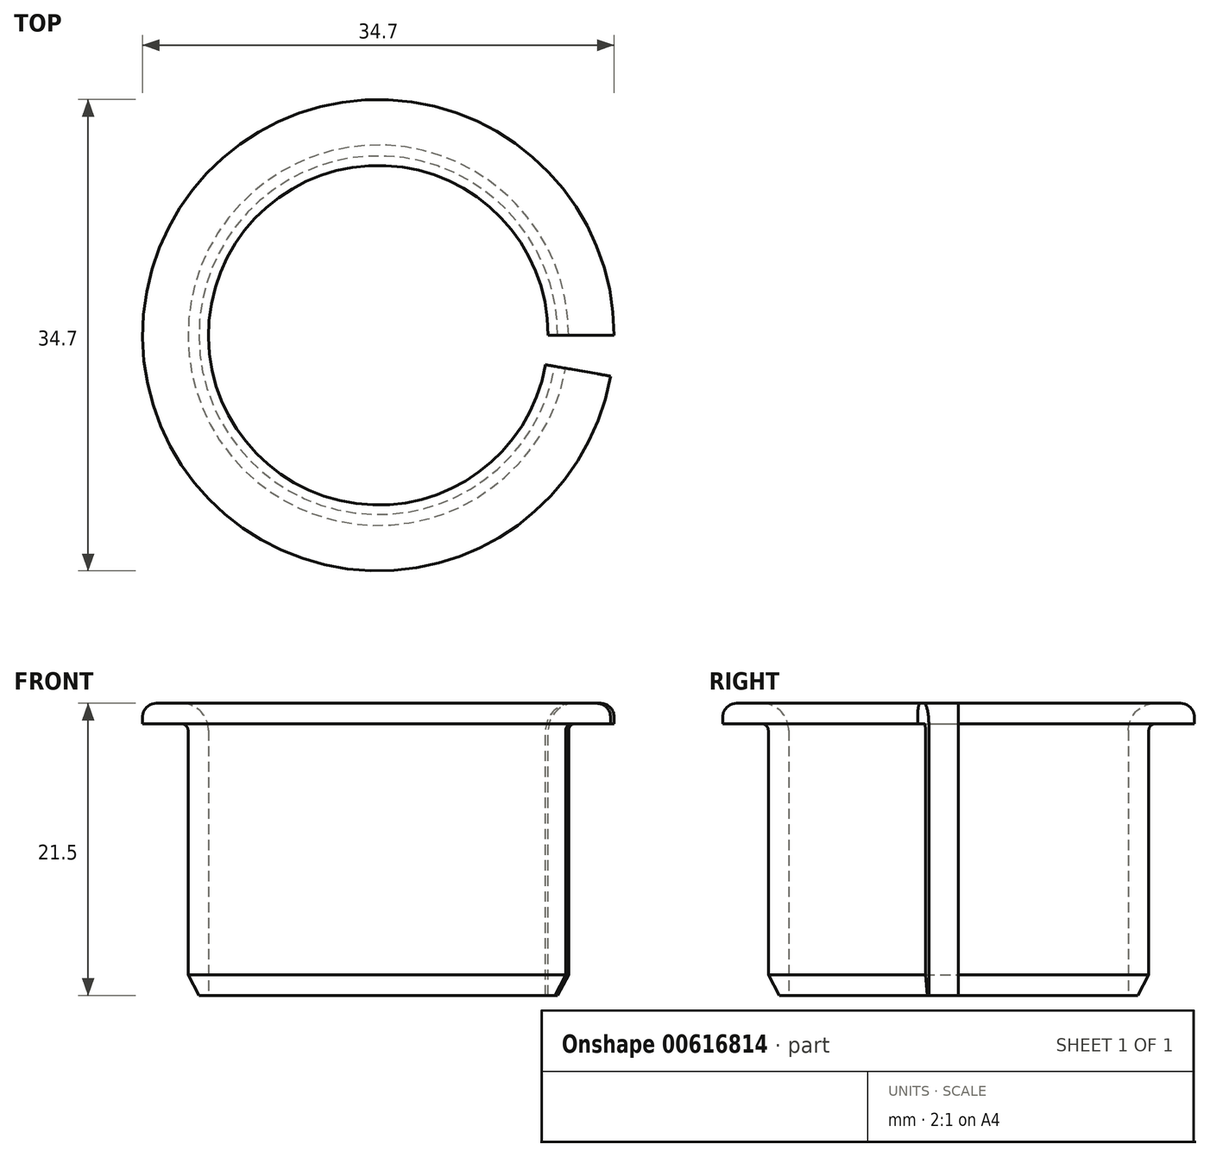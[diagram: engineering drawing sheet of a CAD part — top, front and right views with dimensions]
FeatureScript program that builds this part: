
annotation { "Feature Type Name" : "Feature", "Feature Type Description" : "" }
export const myFeature = defineFeature(function(context is Context, id is Id, definition is map)
    precondition{}
    {
        {
            var Q0;
            Q0=qCreatedBy(makeId("Front.planeOp"),FACE);
            var sketch = newSketch(context, id + "F0", { "sketchPlane" : qUnion([Q0])});
            skLineSegment(sketch, "E0", {"start": v(12.5, 0) * mm, "end": v(12.5, 19.5) * mm});
            skLineSegment(sketch, "E1", {"start": v(14.5, 21.5) * mm, "end": v(16.35, 21.5) * mm});
            skLineSegment(sketch, "E2", {"start": v(17.35, 20.5) * mm, "end": v(17.35, 20) * mm});
            skLineSegment(sketch, "E3", {"start": v(17.35, 20) * mm, "end": v(14.5, 20) * mm});
            skLineSegment(sketch, "E4", {"start": v(14, 19.5) * mm, "end": v(14, 1.5) * mm});
            skLineSegment(sketch, "E5", {"start": v(14, 1.5) * mm, "end": v(13.2, 0) * mm});
            skLineSegment(sketch, "E6", {"start": v(13.2, 0) * mm, "end": v(12.5, 0) * mm});
            skLineSegment(sketch, "E7", {"start": v(0, 0) * mm, "end": v(0, 48.77) * mm, "construction": true});
            skPoint(sketch, "E8.visualSharp", {"position": v(17.35, 21.5) * mm});
            skArc(sketch, "E8.filletArc", {"start": v(17.35, 20.5) * mm, "mid": v(17.06, 21.2) * mm, "end": v(16.35, 21.5) * mm});
            skPoint(sketch, "E9.visualSharp", {"position": v(12.5, 21.5) * mm});
            skArc(sketch, "E9.filletArc", {"start": v(14.5, 21.5) * mm, "mid": v(13.09, 20.91) * mm, "end": v(12.5, 19.5) * mm});
            skPoint(sketch, "E10.visualSharp", {"position": v(14, 20) * mm});
            skArc(sketch, "E10.filletArc", {"start": v(14.5, 20) * mm, "mid": v(14.15, 19.85) * mm, "end": v(14, 19.5) * mm});
            skSolve(sketch);
        }
        {
            var Q0;
            Q0=makeQuery(id+"F0.imprint","IMPRINT",FACE,{"disambiguationData":[TD([[makeQuery(id+"F0.imprint","IMPRINT",EDGE,{"derivedFrom":sQuery(id+"F0.wireOp",EDGE,"E0")}),-1.0]])]});
            var Q1;
            Q1=sQuery(id+"F0.wireOp",EDGE,"E7");
            revolve(context, id + "F1", {"surfaceOperationType" : NewSurfaceOperationType.NEW, "entities" : qUnion([Q0]), "axis" : qUnion([Q1]), "revolveType" : RevolveType.ONE_DIRECTION, "angle" : 350 * degree});
        }
    });
